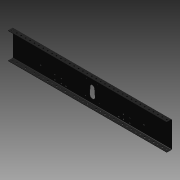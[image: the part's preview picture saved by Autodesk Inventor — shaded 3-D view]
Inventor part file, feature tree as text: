
AUTODESK INVENTOR PART (.ipt)
format: ipt  version: 2014 SP1 (Build 180222100, 222)  size: 430,080 bytes
history: native  units: in
note: dims shown in document units (in); Inventor stores cm internally (conversion verified against a paired STEP export)
features: sketch x8, hole x5, other x4, sheet_metal_op x3, extrude x1
ambient origin geometry x8: Origin, YZ Plane, XZ Plane, XY Plane, X Axis, Y Axis, Z Axis, Center Point
bodies: Solid1 (feature_tree)
feature tree (21):
  sheet_metal_op  "Face1"
  sheet_metal_op  "Flange1"
  hole  "Hole1"  [1 undecoded]
  hole  "Hole2"  [1 undecoded]
  hole  "Hole4"  [1 undecoded]
  hole  "Hole5"  [1 undecoded]
  hole  "Hole7"  [1 undecoded]
  sketch  "Sketch1"  dims[d0=36.0in d1=6.0in]
  other  "Plate1"
  sketch  "Sketch2"  dims[d2=0.09in d3=0.09in]
  other  "Plate2"
  sheet_metal_op  "Bend1"
  sketch  "Sketch3"  dims[d4=0.045in d5=0.18in]
  sketch  "Sketch4"  dims[d6=0.09in d7=1.18in d8=-0.6184in d9=0.09in]
  sketch  "Sketch5"  dims[d10=0.36in d11=0.09in]
  sketch  "Sketch7"  dims[d12=0.09in d13=1.603in]
  sketch  "Sketch8"  dims[d14=0.5in]
  sketch  "Sketch11"  dims[d15=0.625in d16=18.0in d17=36.0in d18=1.625in d19=0.09in d20=0.0in d21=2.5in d22=1.25in d23=3.05in d25=1.176in d26=3.5in d27=1.525in d28=0.206in d29=0.75in d30=0.375in d31=0.25in d32=0.5635in d33=0.09in d34=0.8108in d35=6.3in d36=6.3in d37=1.66in d38=0.266in d39=0.75in d40=0.483in d41=0.25in d42=0.5635in d43=0.09in d44=0.8108in d62=0.5in d63=0.5in d64=14.1732in d66=1.0in d67=0.3937in d69=1.0in d71=0.266in d72=0.75in d73=0.548in d74=0.25in d75=0.5635in d76=0.09in d77=0.8108in d78=12.0in d79=12.0in d80=0.625in d81=4.875in d82=0.266in d83=0.75in d84=0.548in d85=0.25in d86=0.5635in d87=0.09in d88=0.8108in d111=1.5in d112=2.0in d113=9.25in d114=0.25in d115=0.25in d116=0.25in d117=0.25in d118=0.25in d119=0.25in d120=0.25in d121=0.25in d122=0.25in d123=0.25in d124=0.75in d125=0.375in d126=0.25in d127=0.5635in d128=0.09in d129=0.8108in]
  other  "Cut1"
  other  "Definition1"
  extrude  "Extrusion1"  Depth=0.09in
note: 5 required parameter values undecoded (feature->parameter linkage not recoverable at this tier; creation-order binding heuristic only, values carry confidence <= 0.55)
